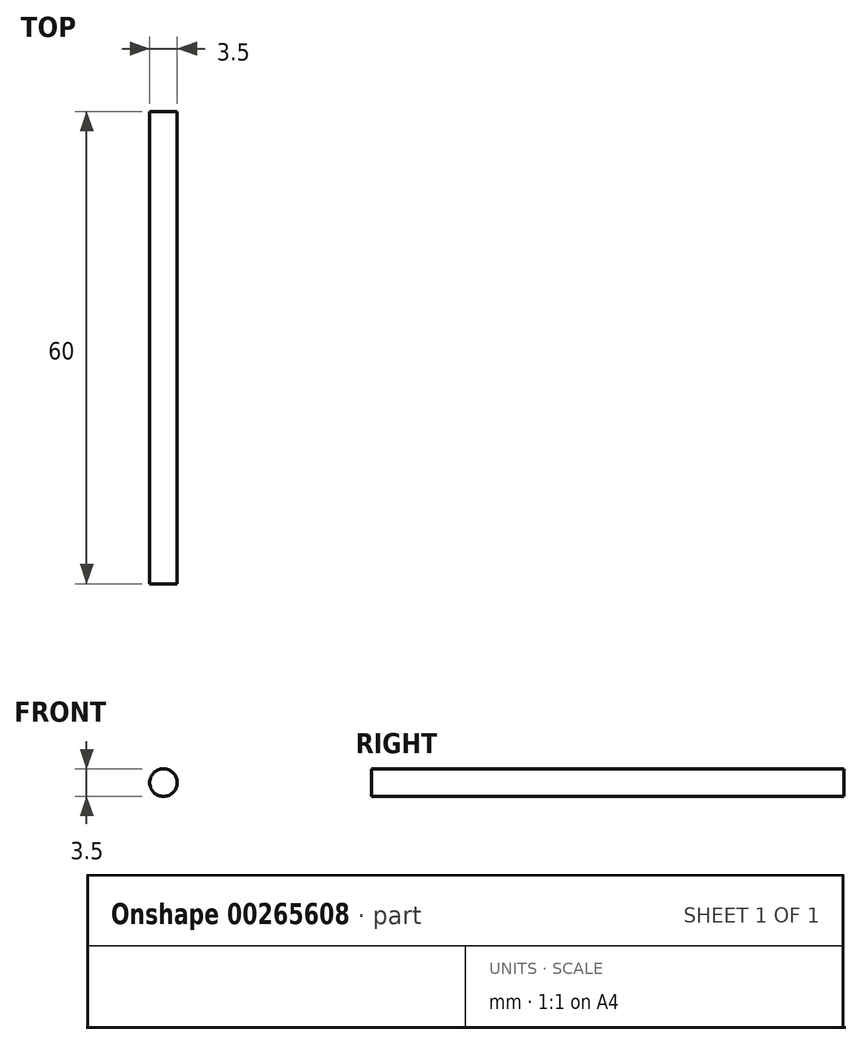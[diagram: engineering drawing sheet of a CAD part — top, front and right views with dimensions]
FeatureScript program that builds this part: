
annotation { "Feature Type Name" : "Feature", "Feature Type Description" : "" }
export const myFeature = defineFeature(function(context is Context, id is Id, definition is map)
    precondition{}
    {
        {
            var Q0;
            Q0=qCreatedBy(makeId("Front.planeOp"),FACE);
            var sketch = newSketch(context, id + "F0", { "sketchPlane" : qUnion([Q0])});
            skCircle(sketch, "E0", {"center": v(0, 0) * mm, "radius": 1.75 * mm});
            skSolve(sketch);
        }
        {
            var Q0;
            Q0=makeQuery(id+"F0.imprint","IMPRINT",FACE,{"disambiguationData":[TD([[makeQuery(id+"F0.imprint","IMPRINT",EDGE,{"derivedFrom":sQuery(id+"F0.wireOp",EDGE,"E0")}),1.0]])]});
            extrude(context, id + "F1", {"entities" : qUnion([Q0]), "depth" : 60 * mm});
        }
    });
